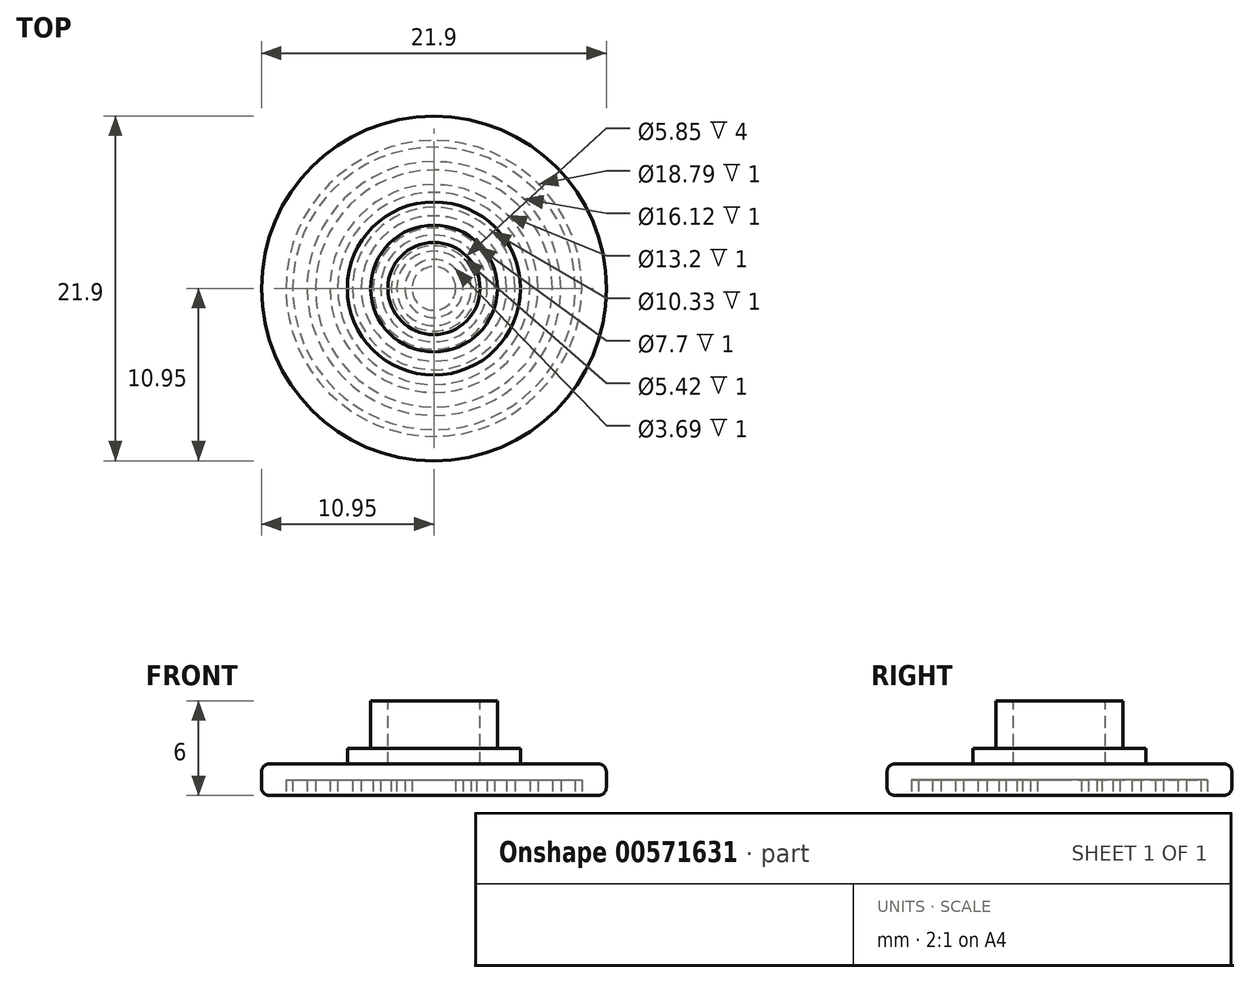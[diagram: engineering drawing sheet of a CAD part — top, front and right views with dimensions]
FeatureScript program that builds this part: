
annotation { "Feature Type Name" : "Feature", "Feature Type Description" : "" }
export const myFeature = defineFeature(function(context is Context, id is Id, definition is map)
    precondition{}
    {
        {
            var Q0;
            Q0=qCreatedBy(makeId("Top.planeOp"),FACE);
            var sketch = newSketch(context, id + "F0", { "sketchPlane" : qUnion([Q0])});
            skCircle(sketch, "E0", {"center": v(0, 0) * mm, "radius": 0.07 * mm});
            skCircle(sketch, "E1", {"center": v(0, 0) * mm, "radius": 10.95 * mm});
            skSolve(sketch);
        }
        {
            var Q0;
            Q0=qCreatedBy(makeId("Top.planeOp"),FACE);
            var sketch = newSketch(context, id + "F1", { "sketchPlane" : qUnion([Q0])});
            skCircle(sketch, "E2", {"center": v(0, 0) * mm, "radius": 5.5 * mm});
            skSolve(sketch);
        }
        {
            var Q0;
            Q0=qCreatedBy(makeId("Top.planeOp"),FACE);
            var sketch = newSketch(context, id + "F2", { "sketchPlane" : qUnion([Q0])});
            skCircle(sketch, "E3", {"center": v(0, 0) * mm, "radius": 4.03 * mm});
            skSolve(sketch);
        }
        {
            var Q0;
            Q0=qSketchRegion(id+"F0",true);
            extrude(context, id + "F3", {"entities" : qUnion([Q0]), "depth" : 2 * mm});
        }
        {
            var Q0;
            Q0=qSketchRegion(id+"F1",true);
            extrude(context, id + "F4", {"entities" : qUnion([Q0]), "operationType" : NewBodyOperationType.ADD, "depth" : 3 * mm});
        }
        {
            var Q0;
            Q0=qSketchRegion(id+"F2",true);
            extrude(context, id + "F5", {"entities" : qUnion([Q0]), "operationType" : NewBodyOperationType.ADD, "depth" : 6 * mm});
        }
        {
            var Q0;
            Q0=makeQuery(id+"F3.opExtrude","SWEPT_FACE",FACE,{"disambiguationData":[OSD([sQuery(id+"F0.wireOp",EDGE,"E1")])]});
            fillet(context, id + "F6", {"entities" : qUnion([Q0]), "radius" : .5 * mm, "tangentPropagation" : true, "allowEdgeOverflow" : false});
        }
        {
            var Q0;
            Q0=makeQuery(id+"F5.opExtrude","CAP_FACE",FACE,{"disambiguationData":[OSD([sQuery(id+"F2.wireOp",EDGE,"E3")])],"isStart":false});
            var sketch = newSketch(context, id + "F7", { "sketchPlane" : qUnion([Q0])});
            skCircle(sketch, "E4.0", {"center": v(0, 0) * mm, "radius": 2.92 * mm});
            skSolve(sketch);
        }
        {
            var Q0;
            Q0=qSketchRegion(id+"F7",true);
            extrude(context, id + "F8", {"entities" : qUnion([Q0]), "operationType" : NewBodyOperationType.REMOVE, "oppositeDirection" : true, "depth" : 4 * mm});
        }
        {
            var Q0;
            Q0=makeQuery(id+"F4.boolean.opBoolean","MERGE",FACE,{"derivedFrom":[makeQuery(id+"F3.opExtrude","CAP_FACE",FACE,{"disambiguationData":[OSD([sQuery(id+"F0.wireOp",EDGE,"E0"),sQuery(id+"F0.wireOp",EDGE,"E1")])],"isStart":true}),makeQuery(id+"F4.opExtrude","CAP_FACE",FACE,{"disambiguationData":[OSD([sQuery(id+"F1.wireOp",EDGE,"E2")])],"isStart":true})]});
            var sketch = newSketch(context, id + "F9", { "sketchPlane" : qUnion([Q0])});
            skCircle(sketch, "E5", {"center": v(0, 0) * mm, "radius": 9.4 * mm});
            skCircle(sketch, "E6", {"center": v(0, 0) * mm, "radius": 8.97 * mm});
            skCircle(sketch, "E7", {"center": v(0, 0) * mm, "radius": 8.06 * mm});
            skCircle(sketch, "E8", {"center": v(0, 0) * mm, "radius": 7.52 * mm});
            skCircle(sketch, "E9", {"center": v(0, 0) * mm, "radius": 6.6 * mm});
            skCircle(sketch, "E10", {"center": v(0, 0) * mm, "radius": 6.1 * mm});
            skCircle(sketch, "E11", {"center": v(0, 0) * mm, "radius": 5.16 * mm});
            skCircle(sketch, "E12", {"center": v(0, 0) * mm, "radius": 4.62 * mm});
            skCircle(sketch, "E13", {"center": v(0, 0) * mm, "radius": 3.85 * mm});
            skCircle(sketch, "E14", {"center": v(0, 0) * mm, "radius": 3.38 * mm});
            skCircle(sketch, "E15", {"center": v(0, 0) * mm, "radius": 2.7 * mm});
            skCircle(sketch, "E16", {"center": v(0, 0) * mm, "radius": 2.37 * mm});
            skCircle(sketch, "E17", {"center": v(0, 0) * mm, "radius": 1.85 * mm});
            skCircle(sketch, "E18", {"center": v(0, 0) * mm, "radius": 1.39 * mm});
            skSolve(sketch);
        }
        {
            var Q0;
            Q0 = qSketchRegion(id + "F9", true);
            var Q1;
            Q1=makeQuery(id+"F9.imprint","IMPRINT",FACE,{"disambiguationData":[TD([[makeQuery(id+"F9.imprint","IMPRINT",EDGE,{"derivedFrom":sQuery(id+"F9.wireOp",EDGE,"E7")}),1.0]])]});
            var Q2;
            Q2=makeQuery(id+"F9.imprint","IMPRINT",FACE,{"disambiguationData":[TD([[makeQuery(id+"F9.imprint","IMPRINT",EDGE,{"derivedFrom":sQuery(id+"F9.wireOp",EDGE,"E9")}),1.0]])]});
            var Q3;
            Q3=makeQuery(id+"F9.imprint","IMPRINT",FACE,{"disambiguationData":[TD([[makeQuery(id+"F9.imprint","IMPRINT",EDGE,{"derivedFrom":sQuery(id+"F9.wireOp",EDGE,"E11")}),1.0]])]});
            var Q4;
            Q4=makeQuery(id+"F9.imprint","IMPRINT",FACE,{"disambiguationData":[TD([[makeQuery(id+"F9.imprint","IMPRINT",EDGE,{"derivedFrom":sQuery(id+"F9.wireOp",EDGE,"E13")}),1.0]])]});
            var Q5;
            Q5=makeQuery(id+"F9.imprint","IMPRINT",FACE,{"disambiguationData":[TD([[makeQuery(id+"F9.imprint","IMPRINT",EDGE,{"derivedFrom":sQuery(id+"F9.wireOp",EDGE,"E15")}),1.0]])]});
            var Q6;
            Q6=makeQuery(id+"F9.imprint","IMPRINT",FACE,{"disambiguationData":[TD([[makeQuery(id+"F9.imprint","IMPRINT",EDGE,{"derivedFrom":sQuery(id+"F9.wireOp",EDGE,"E17")}),1.0]])]});
            extrude(context, id + "F10", {"entities" : qUnion([Q0, Q1, Q2, Q3, Q4, Q5, Q6]), "operationType" : NewBodyOperationType.REMOVE, "oppositeDirection" : true, "depth" : 1 * mm, "offsetDistance" : 25 * mm});
        }
    });
